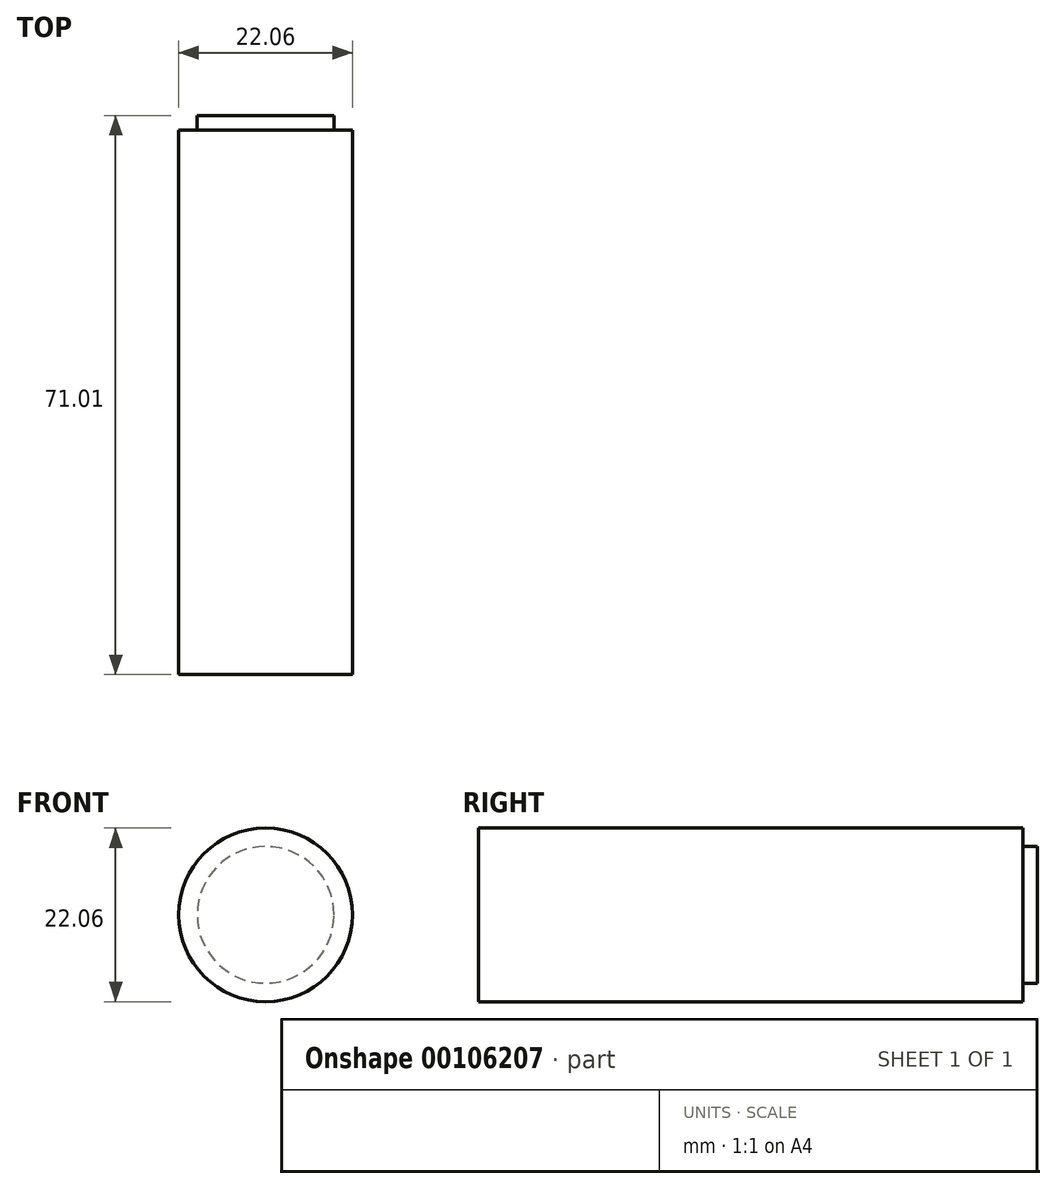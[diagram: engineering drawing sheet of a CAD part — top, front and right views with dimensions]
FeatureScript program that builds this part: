
annotation { "Feature Type Name" : "Feature", "Feature Type Description" : "" }
export const myFeature = defineFeature(function(context is Context, id is Id, definition is map)
    precondition{}
    {
        {
            var Q0;
            Q0=qCreatedBy(makeId("Front.planeOp"),FACE);
            var sketch = newSketch(context, id + "F0", { "sketchPlane" : qUnion([Q0])});
            skCircle(sketch, "E0", {"center": v(0, 0) * mm, "radius": 11.03 * mm});
            skSolve(sketch);
        }
        {
            var Q0;
            Q0 = qSketchRegion(id + "F0", true);
            extrude(context, id + "F1", {"entities" : qUnion([Q0]), "depth" : 69.15 * mm});
        }
        {
            var Q0;
            Q0=makeQuery(id+"F1.opExtrude","CAP_FACE",FACE,{"disambiguationData":[OSD([sQuery(id+"F0.wireOp",EDGE,"E0")])],"isStart":true});
            var sketch = newSketch(context, id + "F2", { "sketchPlane" : qUnion([Q0])});
            skCircle(sketch, "E1", {"center": v(0, 0) * mm, "radius": 8.69 * mm});
            skSolve(sketch);
        }
        {
            var Q0;
            Q0 = qSketchRegion(id + "F2", true);
            extrude(context, id + "F3", {"entities" : qUnion([Q0]), "operationType" : NewBodyOperationType.ADD, "depth" : 1.86 * mm});
        }
    });
